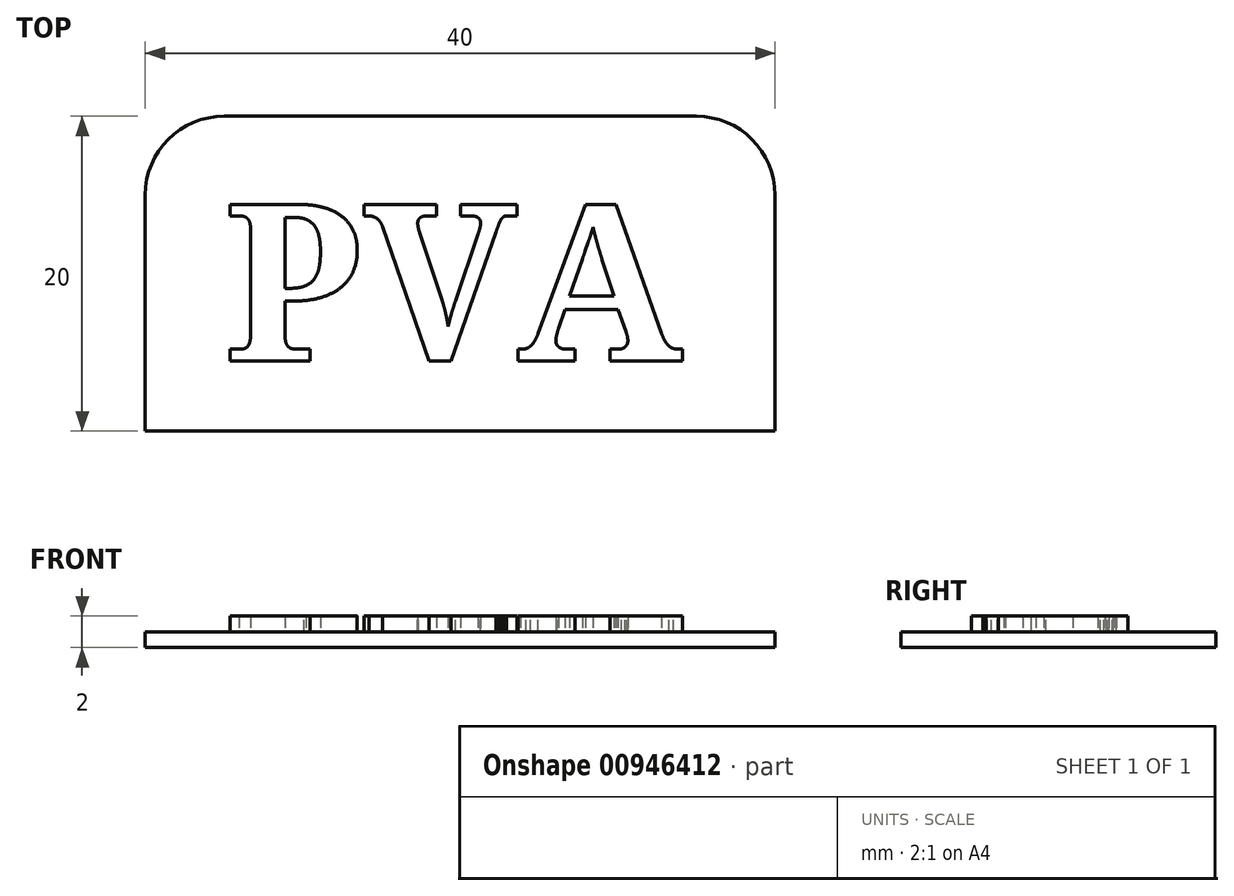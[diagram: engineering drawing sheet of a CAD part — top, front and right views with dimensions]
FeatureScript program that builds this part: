
annotation { "Feature Type Name" : "Feature", "Feature Type Description" : "" }
export const myFeature = defineFeature(function(context is Context, id is Id, definition is map)
    precondition{}
    {
        {
            var Q0;
            Q0=qCreatedBy(makeId("Top.planeOp"),FACE);
            var sketch = newSketch(context, id + "F0", { "sketchPlane" : qUnion([Q0])});
            skLineSegment(sketch, "E0.bottom", {"start": v(-20, 10) * mm, "end": v(20, 10) * mm});
            skLineSegment(sketch, "E0.top", {"start": v(-20, -10) * mm, "end": v(20, -10) * mm});
            skLineSegment(sketch, "E0.left", {"start": v(-20, 10) * mm, "end": v(-20, -10) * mm});
            skLineSegment(sketch, "E0.right", {"start": v(20, 10) * mm, "end": v(20, -10) * mm});
            skPoint(sketch, "E0.middle", {"position": v(0, 0) * mm});
            skSolve(sketch);
        }
        {
            var Q0;
            Q0=makeQuery(id+"F0.imprint","IMPRINT",FACE,{"disambiguationData":[TD([[makeQuery(id+"F0.imprint","IMPRINT",EDGE,{"derivedFrom":sQuery(id+"F0.wireOp",EDGE,"E0.bottom")}),-1.0]])]});
            extrude(context, id + "F1", {"entities" : qUnion([Q0]), "depth" : 1 * mm, "offsetDistance" : 25 * mm});
        }
        {
            var Q0;
            Q0=makeQuery(id+"F1.opExtrude","CAP_FACE",FACE,{"disambiguationData":[OSD([sQuery(id+"F0.wireOp",EDGE,"E0.bottom"),sQuery(id+"F0.wireOp",EDGE,"E0.top"),sQuery(id+"F0.wireOp",EDGE,"E0.left"),sQuery(id+"F0.wireOp",EDGE,"E0.right")])],"isStart":false});
            var sketch = newSketch(context, id + "F2", { "sketchPlane" : qUnion([Q0])});
            skText(sketch, "E1", { "text": "PVA", "fontName": "NotoSerif-Bold.ttf"});
            const initialGuessF2  = {"E1": [-0.015, -0.00554, 1, 0, 0.01003]};
            skSetInitialGuess(sketch, initialGuessF2);
            skSolve(sketch);
        }
        {
            var Q0;
            Q0=qSketchRegion(id+"F2",true);
            extrude(context, id + "F3", {"entities" : qUnion([Q0]), "operationType" : NewBodyOperationType.ADD, "depth" : 1 * mm, "offsetDistance" : 25 * mm});
        }
        {
            var Q0;
            Q0=makeQuery(id+"F1.opExtrude","SWEPT_EDGE",EDGE,{"disambiguationData":[OSD([sQuery(id+"F0.wireOp",EDGE,"E0.bottom"),sQuery(id+"F0.wireOp",EDGE,"E0.left")])]});
            var Q1;
            Q1=makeQuery(id+"F1.opExtrude","SWEPT_EDGE",EDGE,{"disambiguationData":[OSD([sQuery(id+"F0.wireOp",EDGE,"E0.bottom"),sQuery(id+"F0.wireOp",EDGE,"E0.right")])]});
            fillet(context, id + "F4", {"entities" : qUnion([Q0, Q1]), "radius" : 5 * mm, "tangentPropagation" : true, "allowEdgeOverflow" : false});
        }
    });
